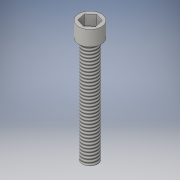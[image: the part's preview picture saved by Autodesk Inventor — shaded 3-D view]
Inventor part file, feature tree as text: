
AUTODESK INVENTOR PART (.ipt)
format: ipt  version: 2016 SP1 (Build 200210100, 210)  size: 118,272 bytes
history: native  units: in
note: dims shown in document units (in); Inventor stores cm internally (conversion verified against a paired STEP export)
features: extrude x3, sketch x3, thread x1
ambient origin geometry x8: Origin, YZ Plane, XZ Plane, XY Plane, X Axis, Y Axis, Z Axis, Center Point
bodies: Solid1 (feature_tree)
feature tree (7):
  extrude  "Extrusion1"  Depth=0.25in
  thread  "Thread1"  [1 undecoded]
  extrude  "Extrusion2"  Depth=0.25in
  extrude  "Extrusion3"  Depth=0.25in
  sketch  "Sketch1"  dims[d0=1.75in d1=0.0in d2=0.25in d3=1.0in d4=0.0in]
  sketch  "Sketch2"  dims[d5=0.25in d6=0.0in d7=0.375in]
  sketch  "Sketch3"  dims[d8=0.17in d9=0.0in d10=0.25in]
note: 1 required parameter value undecoded (feature->parameter linkage not recoverable at this tier; creation-order binding heuristic only, values carry confidence <= 0.55)
